# Revit family: M-5_GENERADO
name_source: partatom
category: Equipos mecánicos
revit_build: Autodesk Revit 2014 (Build: 20130308_1515(x64)
units: mm (PartAtom-declared; Revit-internal decimal feet)

## types (1)
- Potato peeler M-5  230/50-60/1
    Comentarios de tipo = 5 Kg. / 11 pounds load per cycle.
    Cycle = 50 Hz
    Depth = 367 mm  [stored 1.20407 ft]
    Descripción = Potato peeler M-5  230/50-60/1
    Electric Connection Type = EU
    FL Amps = 2 A
    Fabricante = SAMMIC S.L.
    Foodservice Equipment Identifier = Sí
    Height = 490 mm  [stored 1.60761 ft]
    Modelo = 1000565
    Revision Code = 1
    Specification by Manufacturer = Commercial stainless steel construction potato peeler suitable for reduced space areas.
Also suitable to peel carrots and other similar products.
    URL = https://www.sammic.com
    URL Cutsheet = http://www.sammic.com
    Volts = 230 V
    Weight in Pounds = 34.2
    Width = 333 mm  [stored 1.09252 ft]

note: [stored X ft] marks values corroborated as IEEE doubles in the binary element streams (Revit-internal decimal feet)
